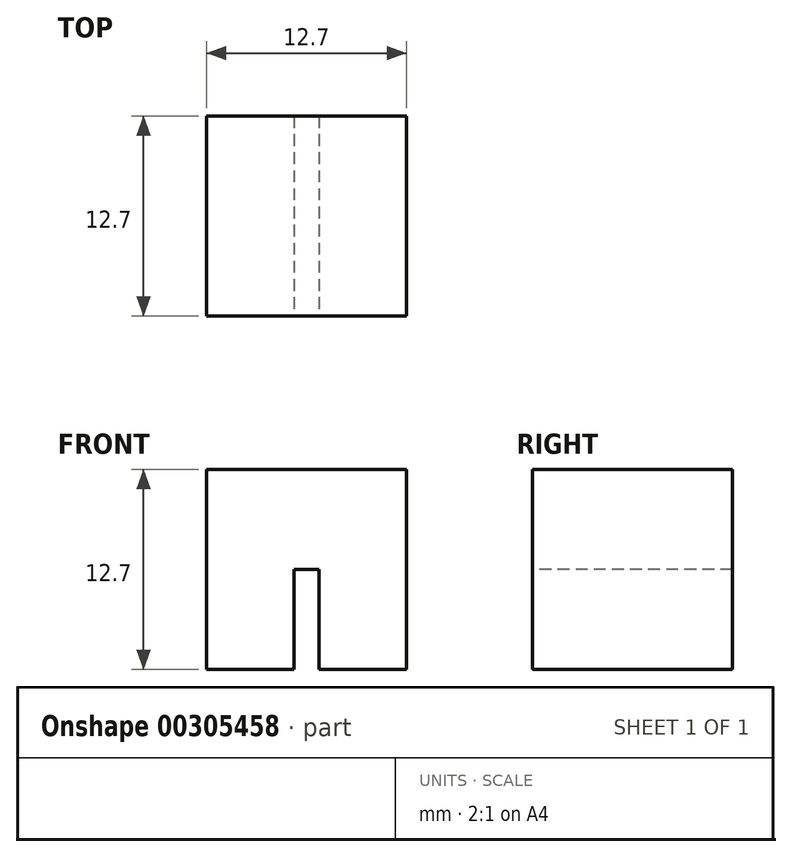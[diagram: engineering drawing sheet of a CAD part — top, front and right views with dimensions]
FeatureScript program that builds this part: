
annotation { "Feature Type Name" : "Feature", "Feature Type Description" : "" }
export const myFeature = defineFeature(function(context is Context, id is Id, definition is map)
    precondition{}
    {
        {
            var Q0;
            Q0=qCreatedBy(makeId("Top.planeOp"),FACE);
            var sketch = newSketch(context, id + "F0", { "sketchPlane" : qUnion([Q0])});
            skLineSegment(sketch, "E0.bottom", {"start": v(-6.35, 6.35) * mm, "end": v(6.35, 6.35) * mm});
            skLineSegment(sketch, "E0.top", {"start": v(-6.35, -6.35) * mm, "end": v(6.35, -6.35) * mm});
            skLineSegment(sketch, "E0.left", {"start": v(-6.35, 6.35) * mm, "end": v(-6.35, -6.35) * mm});
            skLineSegment(sketch, "E0.right", {"start": v(6.35, 6.35) * mm, "end": v(6.35, -6.35) * mm});
            skPoint(sketch, "E1", {"position": v(0, 6.35) * mm});
            skPoint(sketch, "E2", {"position": v(6.35, 0) * mm});
            skSolve(sketch);
        }
        {
            var Q0;
            Q0=makeQuery(id+"F0.imprint","IMPRINT",FACE,{"disambiguationData":[TD([[makeQuery(id+"F0.imprint","IMPRINT",EDGE,{"derivedFrom":sQuery(id+"F0.wireOp",EDGE,"E0.bottom")}),-1.0]])]});
            extrude(context, id + "F1", {"entities" : qUnion([Q0]), "depth" : 12.7 * mm});
        }
        {
            var Q0;
            Q0=makeQuery(id+"F1.opExtrude","SWEPT_FACE",FACE,{"disambiguationData":[OSD([sQuery(id+"F0.wireOp",EDGE,"E0.top")])]});
            var sketch = newSketch(context, id + "F2", { "sketchPlane" : qUnion([Q0])});
            skLineSegment(sketch, "E3.bottom", {"start": v(-0.8, 6.35) * mm, "end": v(0.8, 6.35) * mm});
            skLineSegment(sketch, "E3.top", {"start": v(-0.8, 0) * mm, "end": v(0.8, 0) * mm});
            skLineSegment(sketch, "E3.left", {"start": v(-0.8, 6.35) * mm, "end": v(-0.8, 0) * mm});
            skLineSegment(sketch, "E3.right", {"start": v(0.8, 6.35) * mm, "end": v(0.8, 0) * mm});
            skPoint(sketch, "E4", {"position": v(0, 6.35) * mm});
            skSolve(sketch);
        }
        {
            var Q0;
            Q0=makeQuery(id+"F2.imprint","IMPRINT",FACE,{"disambiguationData":[TD([[makeQuery(id+"F2.imprint","IMPRINT",EDGE,{"derivedFrom":sQuery(id+"F2.wireOp",EDGE,"E3.bottom")}),-1.0]])]});
            var Q1;
            Q1=makeQuery(id+"F1.opExtrude","SWEPT_FACE",FACE,{"disambiguationData":[OSD([sQuery(id+"F0.wireOp",EDGE,"E0.bottom")])]});
            extrude(context, id + "F3", {"entities" : qUnion([Q0]), "operationType" : NewBodyOperationType.REMOVE, "endBound" : BoundingType.UP_TO_SURFACE, "oppositeDirection" : true, "endBoundEntityFace" : qUnion([Q1]), "depth" : 25.4 * mm});
        }
    });
